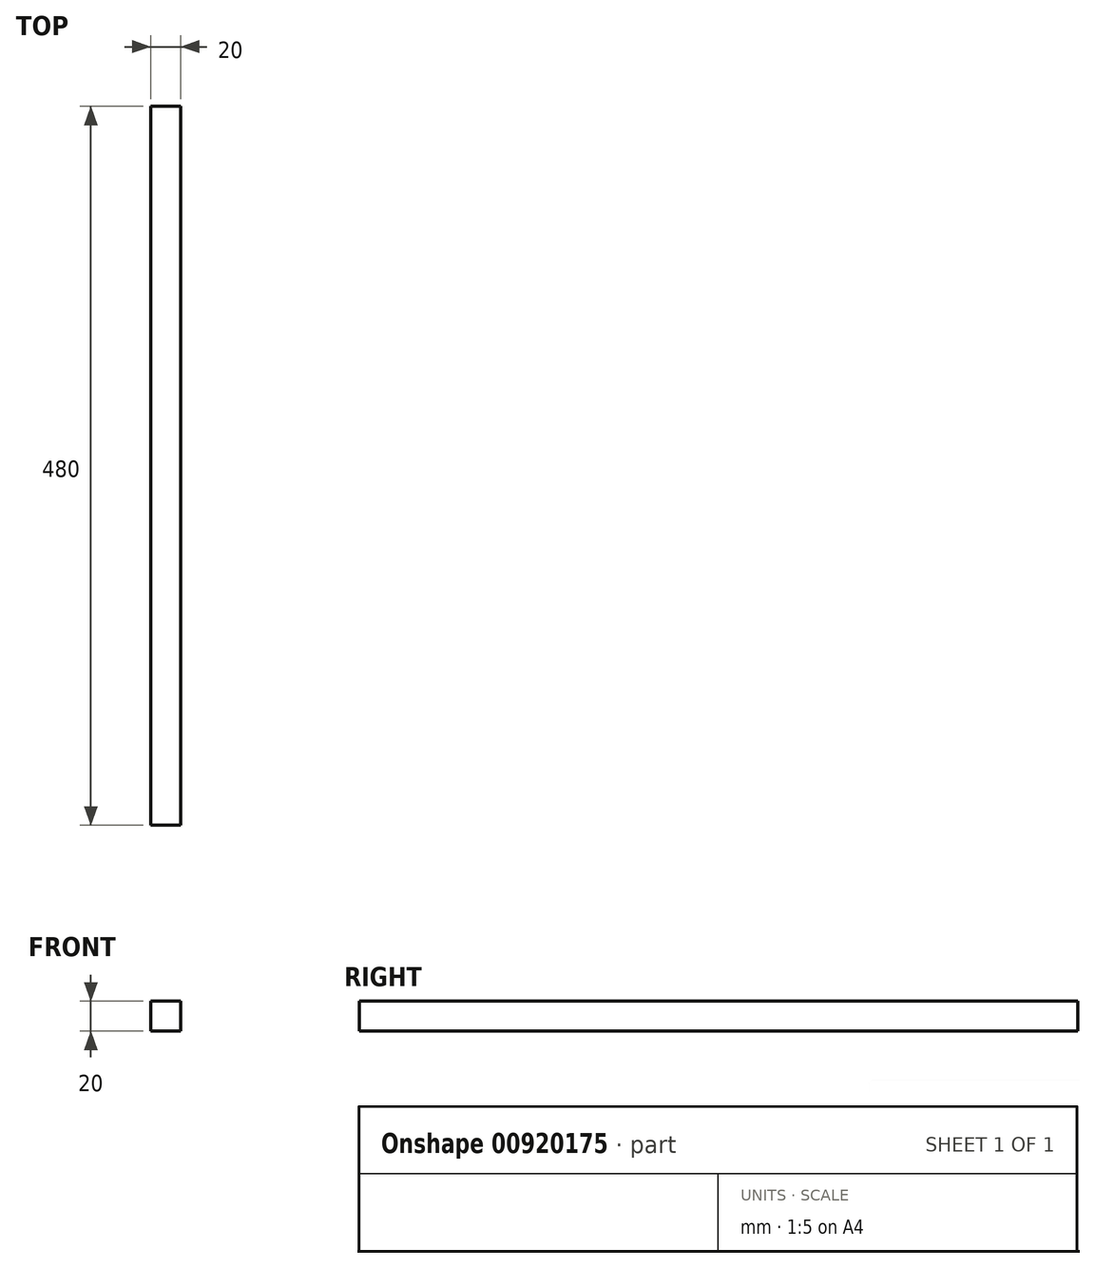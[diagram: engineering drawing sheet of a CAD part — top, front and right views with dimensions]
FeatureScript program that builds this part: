
annotation { "Feature Type Name" : "Feature", "Feature Type Description" : "" }
export const myFeature = defineFeature(function(context is Context, id is Id, definition is map)
    precondition{}
    {
        {
            var Q0;
            Q0=qCreatedBy(makeId("Front.planeOp"),FACE);
            var sketch = newSketch(context, id + "F0", { "sketchPlane" : qUnion([Q0])});
            skLineSegment(sketch, "E0.bottom", {"start": v(-1.9, 12.82) * mm, "end": v(18.1, 12.82) * mm});
            skLineSegment(sketch, "E0.top", {"start": v(-1.9, -7.18) * mm, "end": v(18.1, -7.18) * mm});
            skLineSegment(sketch, "E0.left", {"start": v(-1.9, 12.82) * mm, "end": v(-1.9, -7.18) * mm});
            skLineSegment(sketch, "E0.right", {"start": v(18.1, 12.82) * mm, "end": v(18.1, -7.18) * mm});
            skSolve(sketch);
        }
        {
            var Q0;
            Q0=qSketchRegion(id+"F0",true);
            extrude(context, id + "F1", {"entities" : qUnion([Q0]), "depth" : 480 * mm, "offsetDistance" : 25 * mm});
        }
    });
